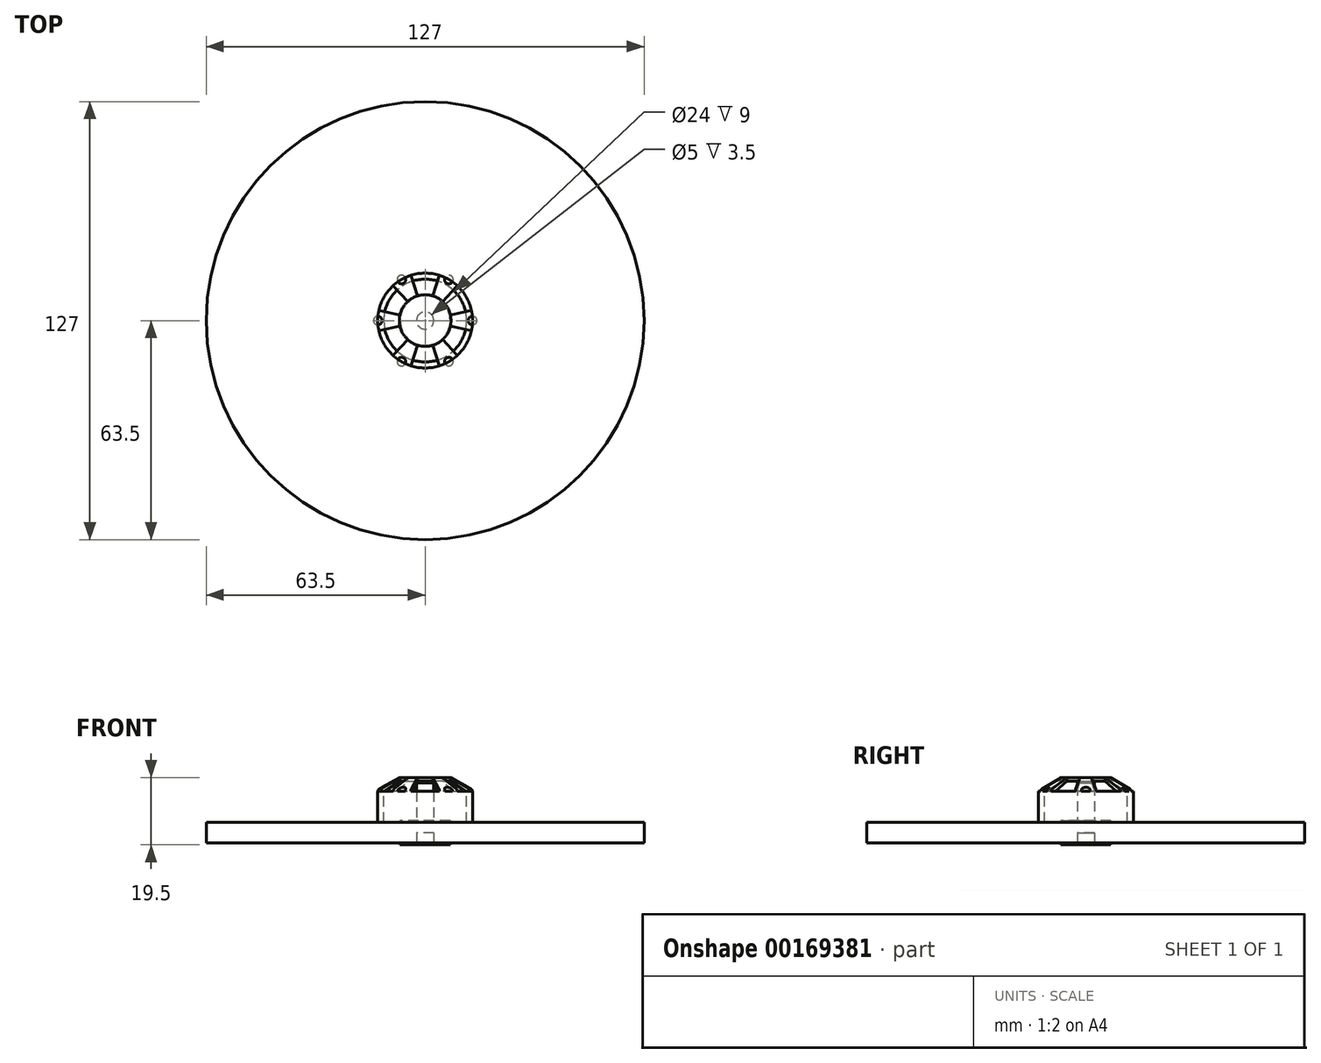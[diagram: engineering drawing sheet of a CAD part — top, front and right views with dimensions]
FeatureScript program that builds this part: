
annotation { "Feature Type Name" : "Feature", "Feature Type Description" : "" }
export const myFeature = defineFeature(function(context is Context, id is Id, definition is map)
    precondition{}
    {
        {
            var Q0;
            Q0=qCreatedBy(makeId("Top.planeOp"),FACE);
            var sketch = newSketch(context, id + "F0", { "sketchPlane" : qUnion([Q0])});
            skCircle(sketch, "E0", {"center": v(0, 0) * mm, "radius": 13.75 * mm});
            skSolve(sketch);
        }
        {
            var Q0;
            Q0=qSketchRegion(id+"F0",true);
            extrude(context, id + "F1", {"entities" : qUnion([Q0]), "depth" : 16 * mm});
        }
        {
            var Q0;
            Q0=makeQuery(id+"F1.opExtrude","CAP_EDGE",EDGE,{"disambiguationData":[OSD([sQuery(id+"F0.wireOp",EDGE,"E0")])],"isStart":false});
            chamfer(context, id + "F2", {"entities" : qUnion([Q0]), "chamferType" : ChamferType.TWO_OFFSETS, "width1" : 6.25 * mm, "oppositeDirection" : false, "width2" : 3.5 * mm, "tangentPropagation" : true});
        }
        {
            var Q0;
            Q0=makeQuery(id+"F1.opExtrude","CAP_EDGE",EDGE,{"disambiguationData":[OSD([sQuery(id+"F0.wireOp",EDGE,"E0")])],"isStart":true});
            chamfer(context, id + "F3", {"entities" : qUnion([Q0]), "chamferType" : ChamferType.TWO_OFFSETS, "width1" : 3 * mm, "oppositeDirection" : false, "width2" : 2 * mm, "tangentPropagation" : true});
        }
        {
            var Q0;
            Q0=makeQuery(id+"F1.opExtrude","CAP_FACE",FACE,{"disambiguationData":[OSD([sQuery(id+"F0.wireOp",EDGE,"E0")])],"isStart":false});
            var sketch = newSketch(context, id + "F4", { "sketchPlane" : qUnion([Q0])});
            skArc(sketch, "E1", {"start": v(2.25, 7.15) * mm, "mid": v(0, 7.5) * mm, "end": v(-2.25, 7.15) * mm});
            skArc(sketch, "E2", {"start": v(4.13, 13.12) * mm, "mid": v(0, 13.75) * mm, "end": v(-4.13, 13.12) * mm});
            skLineSegment(sketch, "E3", {"start": v(0, 0) * mm, "end": v(-2.25, 7.15) * mm, "construction": true});
            skLineSegment(sketch, "E4", {"start": v(0, 0) * mm, "end": v(2.25, 7.15) * mm, "construction": true});
            skLineSegment(sketch, "E5", {"start": v(-2.25, 7.15) * mm, "end": v(-4.12, 13.12) * mm});
            skLineSegment(sketch, "E6", {"start": v(2.25, 7.15) * mm, "end": v(4.12, 13.12) * mm});
            skLineSegment(sketch, "E7.1.0", {"start": v(-5.07, 5.53) * mm, "end": v(-9.3, 10.13) * mm});
            skLineSegment(sketch, "E7.1.1", {"start": v(-7.32, 1.63) * mm, "end": v(-13.42, 2.99) * mm});
            skLineSegment(sketch, "E7.1.2", {"start": v(0, 0) * mm, "end": v(-7.32, 1.63) * mm, "construction": true});
            skLineSegment(sketch, "E7.1.3", {"start": v(0, 0) * mm, "end": v(-5.07, 5.53) * mm, "construction": true});
            skArc(sketch, "E7.1.4", {"start": v(-9.3, 10.13) * mm, "mid": v(-11.9, 6.88) * mm, "end": v(-13.42, 2.99) * mm});
            skArc(sketch, "E7.1.5", {"start": v(-5.07, 5.53) * mm, "mid": v(-6.5, 3.75) * mm, "end": v(-7.32, 1.63) * mm});
            skLineSegment(sketch, "E7.2.0", {"start": v(-7.32, -1.63) * mm, "end": v(-13.42, -2.99) * mm});
            skLineSegment(sketch, "E7.2.1", {"start": v(-5.07, -5.53) * mm, "end": v(-9.3, -10.13) * mm});
            skLineSegment(sketch, "E7.2.2", {"start": v(0, 0) * mm, "end": v(-5.07, -5.53) * mm, "construction": true});
            skLineSegment(sketch, "E7.2.3", {"start": v(0, 0) * mm, "end": v(-7.32, -1.63) * mm, "construction": true});
            skArc(sketch, "E7.2.4", {"start": v(-13.42, -2.99) * mm, "mid": v(-11.9, -6.87) * mm, "end": v(-9.3, -10.13) * mm});
            skArc(sketch, "E7.2.5", {"start": v(-7.32, -1.63) * mm, "mid": v(-6.5, -3.75) * mm, "end": v(-5.07, -5.53) * mm});
            skLineSegment(sketch, "E7.3.0", {"start": v(-2.25, -7.15) * mm, "end": v(-4.13, -13.12) * mm});
            skLineSegment(sketch, "E7.3.1", {"start": v(2.25, -7.15) * mm, "end": v(4.12, -13.12) * mm});
            skLineSegment(sketch, "E7.3.2", {"start": v(0, 0) * mm, "end": v(2.25, -7.15) * mm, "construction": true});
            skLineSegment(sketch, "E7.3.3", {"start": v(0, 0) * mm, "end": v(-2.25, -7.15) * mm, "construction": true});
            skArc(sketch, "E7.3.4", {"start": v(-4.13, -13.12) * mm, "mid": v(0, -13.75) * mm, "end": v(4.12, -13.12) * mm});
            skArc(sketch, "E7.3.5", {"start": v(-2.25, -7.15) * mm, "mid": v(0, -7.5) * mm, "end": v(2.25, -7.15) * mm});
            skLineSegment(sketch, "E7.4.0", {"start": v(5.07, -5.53) * mm, "end": v(9.3, -10.13) * mm});
            skLineSegment(sketch, "E7.4.1", {"start": v(7.32, -1.63) * mm, "end": v(13.42, -2.99) * mm});
            skLineSegment(sketch, "E7.4.2", {"start": v(0, 0) * mm, "end": v(7.32, -1.63) * mm, "construction": true});
            skLineSegment(sketch, "E7.4.3", {"start": v(0, 0) * mm, "end": v(5.07, -5.53) * mm, "construction": true});
            skArc(sketch, "E7.4.4", {"start": v(9.3, -10.13) * mm, "mid": v(11.9, -6.88) * mm, "end": v(13.42, -2.99) * mm});
            skArc(sketch, "E7.4.5", {"start": v(5.07, -5.53) * mm, "mid": v(6.5, -3.75) * mm, "end": v(7.32, -1.63) * mm});
            skLineSegment(sketch, "E7.5.0", {"start": v(7.32, 1.63) * mm, "end": v(13.42, 2.99) * mm});
            skLineSegment(sketch, "E7.5.1", {"start": v(5.07, 5.53) * mm, "end": v(9.3, 10.13) * mm});
            skLineSegment(sketch, "E7.5.2", {"start": v(0, 0) * mm, "end": v(5.07, 5.53) * mm, "construction": true});
            skLineSegment(sketch, "E7.5.3", {"start": v(0, 0) * mm, "end": v(7.32, 1.63) * mm, "construction": true});
            skArc(sketch, "E7.5.4", {"start": v(13.42, 2.99) * mm, "mid": v(11.9, 6.88) * mm, "end": v(9.3, 10.13) * mm});
            skArc(sketch, "E7.5.5", {"start": v(7.32, 1.63) * mm, "mid": v(6.5, 3.75) * mm, "end": v(5.07, 5.53) * mm});
            skSolve(sketch);
        }
        {
            var Q0;
            Q0=qSketchRegion(id+"F4",true);
            extrude(context, id + "F5", {"entities" : qUnion([Q0]), "operationType" : NewBodyOperationType.REMOVE, "oppositeDirection" : true, "depth" : 4 * mm});
        }
        {
            var Q0;
            {var subQ0=sQuery(id+"F0.wireOp",EDGE,"E0");var subQ1=makeQuery(id+"F1.opExtrude","SWEPT_FACE",FACE,{"disambiguationData":[OSD([subQ0])]});Q0=makeQuery(id+"F5.boolean.opBoolean","SPLIT",EDGE,{"disambiguationData":[TD([makeQuery(id+"F5.opExtrude","SWEPT_FACE",FACE,{"disambiguationData":[OSD([sQuery(id+"F4.wireOp",EDGE,"E7.4.1")])]})])],"derivedFrom":makeQuery(id+"F2.opChamfer","BLEND_EDGE",EDGE,{"blendedFrom":[makeQuery(id+"F1.opExtrude","CAP_EDGE",EDGE,{"disambiguationData":[OSD([subQ0])],"isStart":false}),subQ1],"blendedInto":[subQ1]})});}
            var Q1;
            {var subQ0=sQuery(id+"F0.wireOp",EDGE,"E0");var subQ1=makeQuery(id+"F1.opExtrude","SWEPT_FACE",FACE,{"disambiguationData":[OSD([subQ0])]});Q1=makeQuery(id+"F5.boolean.opBoolean","SPLIT",EDGE,{"disambiguationData":[TD([makeQuery(id+"F5.opExtrude","SWEPT_FACE",FACE,{"disambiguationData":[OSD([sQuery(id+"F4.wireOp",EDGE,"E6")])]})])],"derivedFrom":makeQuery(id+"F2.opChamfer","BLEND_EDGE",EDGE,{"blendedFrom":[makeQuery(id+"F1.opExtrude","CAP_EDGE",EDGE,{"disambiguationData":[OSD([subQ0])],"isStart":false}),subQ1],"blendedInto":[subQ1]})});}
            var Q2;
            {var subQ0=sQuery(id+"F0.wireOp",EDGE,"E0");var subQ1=makeQuery(id+"F1.opExtrude","SWEPT_FACE",FACE,{"disambiguationData":[OSD([subQ0])]});Q2=makeQuery(id+"F5.boolean.opBoolean","SPLIT",EDGE,{"disambiguationData":[TD([makeQuery(id+"F5.opExtrude","SWEPT_FACE",FACE,{"disambiguationData":[OSD([sQuery(id+"F4.wireOp",EDGE,"E5")])]})])],"derivedFrom":makeQuery(id+"F2.opChamfer","BLEND_EDGE",EDGE,{"blendedFrom":[makeQuery(id+"F1.opExtrude","CAP_EDGE",EDGE,{"disambiguationData":[OSD([subQ0])],"isStart":false}),subQ1],"blendedInto":[subQ1]})});}
            var Q3;
            {var subQ0=sQuery(id+"F0.wireOp",EDGE,"E0");var subQ1=makeQuery(id+"F1.opExtrude","SWEPT_FACE",FACE,{"disambiguationData":[OSD([subQ0])]});Q3=makeQuery(id+"F5.boolean.opBoolean","SPLIT",EDGE,{"disambiguationData":[TD([makeQuery(id+"F5.opExtrude","SWEPT_FACE",FACE,{"disambiguationData":[OSD([sQuery(id+"F4.wireOp",EDGE,"E7.1.1")])]})])],"derivedFrom":makeQuery(id+"F2.opChamfer","BLEND_EDGE",EDGE,{"blendedFrom":[makeQuery(id+"F1.opExtrude","CAP_EDGE",EDGE,{"disambiguationData":[OSD([subQ0])],"isStart":false}),subQ1],"blendedInto":[subQ1]})});}
            var Q4;
            {var subQ0=sQuery(id+"F0.wireOp",EDGE,"E0");var subQ1=makeQuery(id+"F1.opExtrude","SWEPT_FACE",FACE,{"disambiguationData":[OSD([subQ0])]});Q4=makeQuery(id+"F5.boolean.opBoolean","SPLIT",EDGE,{"disambiguationData":[TD([makeQuery(id+"F5.opExtrude","SWEPT_FACE",FACE,{"disambiguationData":[OSD([sQuery(id+"F4.wireOp",EDGE,"E7.2.1")])]})])],"derivedFrom":makeQuery(id+"F2.opChamfer","BLEND_EDGE",EDGE,{"blendedFrom":[makeQuery(id+"F1.opExtrude","CAP_EDGE",EDGE,{"disambiguationData":[OSD([subQ0])],"isStart":false}),subQ1],"blendedInto":[subQ1]})});}
            var Q5;
            {var subQ0=sQuery(id+"F0.wireOp",EDGE,"E0");var subQ1=makeQuery(id+"F1.opExtrude","SWEPT_FACE",FACE,{"disambiguationData":[OSD([subQ0])]});Q5=makeQuery(id+"F5.boolean.opBoolean","SPLIT",EDGE,{"disambiguationData":[TD([makeQuery(id+"F5.opExtrude","SWEPT_FACE",FACE,{"disambiguationData":[OSD([sQuery(id+"F4.wireOp",EDGE,"E7.3.1")])]})])],"derivedFrom":makeQuery(id+"F2.opChamfer","BLEND_EDGE",EDGE,{"blendedFrom":[makeQuery(id+"F1.opExtrude","CAP_EDGE",EDGE,{"disambiguationData":[OSD([subQ0])],"isStart":false}),subQ1],"blendedInto":[subQ1]})});}
            fillet(context, id + "F6", {"entities" : qUnion([Q0, Q1, Q2, Q3, Q4, Q5]), "radius" : 0.75 * mm, "tangentPropagation" : true, "allowEdgeOverflow" : false});
        }
        {
            var Q0;
            Q0=makeQuery(id+"F1.opExtrude","CAP_FACE",FACE,{"disambiguationData":[OSD([sQuery(id+"F0.wireOp",EDGE,"E0")])],"isStart":false});
            var sketch = newSketch(context, id + "F7", { "sketchPlane" : qUnion([Q0])});
            skCircle(sketch, "E8", {"center": v(13.75, 0) * mm, "radius": 1.25 * mm});
            skCircle(sketch, "E9.1.0", {"center": v(6.88, 11.9) * mm, "radius": 1.25 * mm});
            skCircle(sketch, "E9.2.0", {"center": v(-6.87, 11.9) * mm, "radius": 1.25 * mm});
            skCircle(sketch, "E9.3.0", {"center": v(-13.75, 0) * mm, "radius": 1.25 * mm});
            skCircle(sketch, "E9.4.0", {"center": v(-6.88, -11.9) * mm, "radius": 1.25 * mm});
            skCircle(sketch, "E9.5.0", {"center": v(6.88, -11.9) * mm, "radius": 1.25 * mm});
            skPoint(sketch, "E9.center", {"position": v(0, 0) * mm});
            skSolve(sketch);
        }
        {
            var Q0;
            Q0=qSketchRegion(id+"F7",true);
            extrude(context, id + "F8", {"entities" : qUnion([Q0]), "operationType" : NewBodyOperationType.REMOVE, "oppositeDirection" : true, "depth" : 4 * mm});
        }
        {
            var Q0;
            Q0=makeQuery(id+"F1.opExtrude","CAP_FACE",FACE,{"disambiguationData":[OSD([sQuery(id+"F0.wireOp",EDGE,"E0")])],"isStart":true});
            var sketch = newSketch(context, id + "F9", { "sketchPlane" : qUnion([Q0])});
            skArc(sketch, "E10", {"start": v(3, 10.84) * mm, "mid": v(0, 11.25) * mm, "end": v(-3, 10.84) * mm});
            skArc(sketch, "E11", {"start": v(3, 13.42) * mm, "mid": v(0, 13.75) * mm, "end": v(-3, 13.42) * mm});
            skLineSegment(sketch, "E12", {"start": v(-3, 13.42) * mm, "end": v(-3, 10.84) * mm});
            skLineSegment(sketch, "E13", {"start": v(3, 13.42) * mm, "end": v(3, 10.84) * mm});
            skLineSegment(sketch, "E14.1.0", {"start": v(-13.42, 3) * mm, "end": v(-10.84, 3) * mm});
            skArc(sketch, "E14.1.1", {"start": v(-13.42, 3) * mm, "mid": v(-13.75, 0) * mm, "end": v(-13.42, -3) * mm});
            skLineSegment(sketch, "E14.1.2", {"start": v(-13.42, -3) * mm, "end": v(-10.84, -3) * mm});
            skArc(sketch, "E14.1.3", {"start": v(-10.84, 3) * mm, "mid": v(-11.25, 0) * mm, "end": v(-10.84, -3) * mm});
            skLineSegment(sketch, "E14.2.0", {"start": v(-3, -13.42) * mm, "end": v(-3, -10.84) * mm});
            skArc(sketch, "E14.2.1", {"start": v(-3, -13.42) * mm, "mid": v(0, -13.75) * mm, "end": v(3, -13.42) * mm});
            skLineSegment(sketch, "E14.2.2", {"start": v(3, -13.42) * mm, "end": v(3, -10.84) * mm});
            skArc(sketch, "E14.2.3", {"start": v(-3, -10.84) * mm, "mid": v(0, -11.25) * mm, "end": v(3, -10.84) * mm});
            skLineSegment(sketch, "E14.3.0", {"start": v(13.42, -3) * mm, "end": v(10.84, -3) * mm});
            skArc(sketch, "E14.3.1", {"start": v(13.42, -3) * mm, "mid": v(13.75, 0) * mm, "end": v(13.42, 3) * mm});
            skLineSegment(sketch, "E14.3.2", {"start": v(13.42, 3) * mm, "end": v(10.84, 3) * mm});
            skArc(sketch, "E14.3.3", {"start": v(10.84, -3) * mm, "mid": v(11.25, 0) * mm, "end": v(10.84, 3) * mm});
            skSolve(sketch);
        }
        {
            var Q0;
            Q0=qSketchRegion(id+"F9",true);
            extrude(context, id + "F10", {"entities" : qUnion([Q0]), "operationType" : NewBodyOperationType.REMOVE, "oppositeDirection" : true, "depth" : 2.8 * mm});
        }
        {
            var Q0;
            Q0=makeQuery(id+"F10.boolean.opBoolean","COPY",EDGE,{"derivedFrom":makeQuery(id+"F10.opExtrude","CAP_EDGE",EDGE,{"disambiguationData":[OSD([sQuery(id+"F9.wireOp",EDGE,"E10")])],"isStart":false})});
            var Q1;
            Q1=makeQuery(id+"F10.boolean.opBoolean","COPY",EDGE,{"derivedFrom":makeQuery(id+"F10.opExtrude","CAP_EDGE",EDGE,{"disambiguationData":[OSD([sQuery(id+"F9.wireOp",EDGE,"E14.1.3")])],"isStart":false})});
            var Q2;
            Q2=makeQuery(id+"F10.boolean.opBoolean","COPY",EDGE,{"derivedFrom":makeQuery(id+"F10.opExtrude","CAP_EDGE",EDGE,{"disambiguationData":[OSD([sQuery(id+"F9.wireOp",EDGE,"E14.2.3")])],"isStart":false})});
            var Q3;
            Q3=makeQuery(id+"F10.boolean.opBoolean","COPY",EDGE,{"derivedFrom":makeQuery(id+"F10.opExtrude","CAP_EDGE",EDGE,{"disambiguationData":[OSD([sQuery(id+"F9.wireOp",EDGE,"E14.3.3")])],"isStart":false})});
            chamfer(context, id + "F11", {"entities" : qUnion([Q0, Q1, Q2, Q3]), "chamferType" : ChamferType.TWO_OFFSETS, "width1" : 2.75 * mm, "oppositeDirection" : false, "width2" : 1.75 * mm, "tangentPropagation" : true});
        }
        {
            var Q0;
            Q0=qCreatedBy(makeId("Front.planeOp"),FACE);
            var sketch = newSketch(context, id + "F12", { "sketchPlane" : qUnion([Q0])});
            skLineSegment(sketch, "E15", {"start": v(0, 15) * mm, "end": v(-7.5, 15) * mm});
            skLineSegment(sketch, "E16", {"start": v(-7.5, 15) * mm, "end": v(-12, 12) * mm});
            skLineSegment(sketch, "E17", {"start": v(-12, 12) * mm, "end": v(-12, 3) * mm});
            skLineSegment(sketch, "E18", {"start": v(-12, 3) * mm, "end": v(-11, 1.5) * mm});
            skLineSegment(sketch, "E19", {"start": v(-11, 1.5) * mm, "end": v(0, 1.5) * mm});
            skLineSegment(sketch, "E20", {"start": v(0, 1.5) * mm, "end": v(0, 15) * mm});
            skSolve(sketch);
        }
        {
            var Q0;
            Q0=qSketchRegion(id+"F12",true);
            var Q1;
            Q1=sQuery(id+"F12.wireOp",EDGE,"E20");
            revolve(context, id + "F13", {"operationType" : NewBodyOperationType.REMOVE, "entities" : qUnion([Q0]), "axis" : qUnion([Q1]), "revolveType" : RevolveType.FULL, "oppositeDirection" : true});
        }
        {
            var Q0;
            Q0=qCreatedBy(makeId("Top.planeOp"),FACE);
            var sketch = newSketch(context, id + "F14", { "sketchPlane" : qUnion([Q0])});
            skCircle(sketch, "E21", {"center": v(0, 0) * mm, "radius": 7.5 * mm});
            skSolve(sketch);
        }
        {
            var Q0;
            Q0=makeQuery(id+"F14.imprint","IMPRINT",FACE,{"disambiguationData":[TD([[makeQuery(id+"F14.imprint","IMPRINT",EDGE,{"derivedFrom":sQuery(id+"F14.wireOp",EDGE,"E21")}),1.0]])]});
            extrude(context, id + "F15", {"entities" : qUnion([Q0]), "depth" : 3 * mm});
        }
        {
            var Q0;
            Q0=makeQuery(id+"F15.opExtrude","CAP_FACE",FACE,{"disambiguationData":[OSD([sQuery(id+"F14.wireOp",EDGE,"E21")])],"isStart":false});
            var sketch = newSketch(context, id + "F16", { "sketchPlane" : qUnion([Q0])});
            skCircle(sketch, "E22", {"center": v(0, 0) * mm, "radius": 2.5 * mm});
            skSolve(sketch);
        }
        {
            var Q0;
            Q0=makeQuery(id+"F16.imprint","IMPRINT",FACE,{"disambiguationData":[TD([[makeQuery(id+"F16.imprint","IMPRINT",EDGE,{"derivedFrom":sQuery(id+"F16.wireOp",EDGE,"E22")}),1.0]])]});
            extrude(context, id + "F17", {"entities" : qUnion([Q0]), "operationType" : NewBodyOperationType.ADD, "depth" : 11.5 * mm});
        }
        {
            var Q0;
            Q0=qCreatedBy(makeId("Top.planeOp"),FACE);
            var sketch = newSketch(context, id + "F18", { "sketchPlane" : qUnion([Q0])});
            skCircle(sketch, "E23", {"center": v(0, 0) * mm, "radius": 7.25 * mm});
            skCircle(sketch, "E24", {"center": v(0, 0) * mm, "radius": 2.5 * mm});
            skSolve(sketch);
        }
        {
            var Q0;
            Q0=makeQuery(id+"F18.imprint","IMPRINT",FACE,{"disambiguationData":[TD([[makeQuery(id+"F18.imprint","IMPRINT",EDGE,{"derivedFrom":sQuery(id+"F18.wireOp",EDGE,"E23")}),1.0]])]});
            extrude(context, id + "F19", {"entities" : qUnion([Q0]), "endBound" : BoundingType.SYMMETRIC, "depth" : 7 * mm});
        }
        {
            var Q0;
            Q0=qCreatedBy(makeId("Top.planeOp"),FACE);
            var sketch = newSketch(context, id + "F20", { "sketchPlane" : qUnion([Q0])});
            skCircle(sketch, "E25", {"center": v(0, 0) * mm, "radius": 63.5 * mm});
            skCircle(sketch, "E26", {"center": v(0, 0) * mm, "radius": 7.25 * mm});
            skSolve(sketch);
        }
        {
            var Q0;
            Q0=qSketchRegion(id+"F20",true);
            extrude(context, id + "F21", {"entities" : qUnion([Q0]), "operationType" : NewBodyOperationType.ADD, "endBound" : BoundingType.SYMMETRIC, "depth" : 6 * mm});
        }
    });
